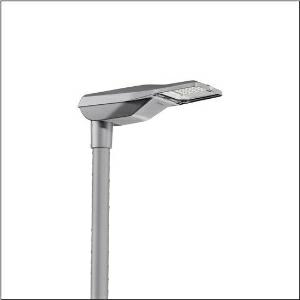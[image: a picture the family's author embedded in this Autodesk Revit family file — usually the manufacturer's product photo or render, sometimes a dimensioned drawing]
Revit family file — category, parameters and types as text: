
# Revit family: streetlight_sl_21_iq_micro___stw1_0a_5xe1e41d08db_39eb
name_source: partatom
category: Lighting Fixtures
units: mm (PartAtom-declared; Revit-internal decimal feet)

## family parameters
Cut with Voids When Loaded = No
Host = Face
Light Source = No
Part Type = Normal
Room Calculation Point = No
Round Connector Dimension = Use Diameter
Shared = No

## types (1)
- --- (1 x LED, 5010 lm, 36.4 W, 4000K)
    Apparent Load = 36 VA
    CIE Flux Codes = 38 75 98 100 100
    Color Rendering = 70
    Color Temperature = 4000K
    Default Elevation = 1800 mm
    Description = Streetlight SL 21 iQ micro, mast luminaire, primary light control with lens, of PMMA, primary optical cover: cover, of toughened safety glass, transparent, light distribution: STW1.0a, light emission: direct distribution, primary light characteristic: asymmetric, installation type: post-top, side-entry, LED, High Power LED, rated luminous flux: 5.010lm, luminous efficacy: 138lm/W, light colour: 740, colour temperature: 4000K, control gear: iQ-Comfort, control: Auto-Match, Temp-Guard, Lumen-Switch, Night-Set, Smart-Wire, Light-Fading, Desk-Remote (wireless, voltage-free reading and setting of iQ features in the workshop via application-optimized NFC function/RFID function), optimised constant luminous flux control (CLO 2.0), pre-setting: linear dimming characteristic, mains connection: 220..240V, AC, 50/60Hz, start of lifetime: 36W, end of service life: 38W, reduction: 16W, luminaire housing, of diecast aluminium, powder-coated, Siteco® metallic grey (DB 702S), corrosivity category C5 mid according to DIN EN ISO 12944, please order mast flange separately, inclination adjustable: 0°, 5°, 10°, 15°, sealing non-destructively replaceable, multi-level sealing system, length: 528mm, width: 235mm, height: 110mm, mast flange for spigot size: 42mm (side-entry): 5XC10008XM4, 60/48mm (side-entry/post-top): 5XC10108XM2, 76/60mm (side-entry/post-top): 5XC10108XM1, protection rating (complete): IP66, insulation class (complete): insulation class II (safety insulation), certification: CE, ENEC, ENEC+, VDE, impact resistance: IK10, permissible operating ambient temperature for outdoor applications: -40..+50°C, standard-compliant lighting for roads and squares, packaging unit: 1 piece

Light Distribution: STW1.0a
    Height = 110 mm
    Lamp = 1 x LED
    Lamp Light Flux = 5010 lm
    Lamp Power = 36.4 W
    Lamp count = 1
    Length = 528 mm
    Luminous efficacy = 138 lm/W
    Manufacturer = Siteco
    ModVariant = No
    Model = 5XE1E41D08DB
    Number of Poles = 1
    OnlyDefault = Yes
    Power Factor = 1
    Product Name = Streetlight SL 21 iQ micro | STW1.0a
    Product group = mast luminaire | pylon top
    ProductGroupID = 6100
    Protection Class = Protection class II
    Protection Degree = IP 66
    RLX_Detail_Level = 1
    RLX_Emergency_Light_Flux = 0 lm
    RLX_Emergency_Type = 0
    RLX_Emergency_Type_DB = No
    RlxData = <blob elided: 99269 chars, md5=e6d32c59>
    Socket = socket
    Standby Power = 0 W
    System Light Flux = 5010 lm
    System Power = 36 W
    Type Comments = factory setting: luminous flux: 100 % | dim-lin: 254 | 715 mA
    Type Image = l_1006881.jpg
    URL = http://relux.com
    VarID = @adj_176903
    Voltage = 0 V
    Weight = 0.00 kg
    Width = 235 mm

## geometry (parser evidence)
native form markers: Blend x4, Sweep x11
no freeform markers — native parametric forms only
